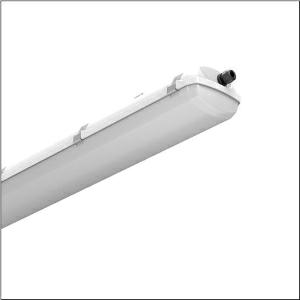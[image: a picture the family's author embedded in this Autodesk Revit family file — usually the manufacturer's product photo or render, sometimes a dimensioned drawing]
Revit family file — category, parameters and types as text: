
# Revit family: monsun_r__ex_51fxb17p670a3g_589b
name_source: partatom
category: Lighting Fixtures
units: mm (PartAtom-declared; Revit-internal decimal feet)

## family parameters
Cut with Voids When Loaded = No
Host = Face
Light Source = No
Part Type = Normal
Room Calculation Point = No
Round Connector Dimension = Use Diameter
Shared = No

## types (1)
- --- (1 x LED, 7310 lm, 44 W, 6500K)
    Apparent Load = 44 VA
    CIE Flux Codes = 61 86 97 100 100
    Color Rendering = 80
    Color Temperature = 6500K
    Default Elevation = 1800 mm
    Description = Monsun® Ex, damp-proof luminaire, primary optical cover: cover, of PC, UV-stabilised, opal, light emission: direct distribution, primary light characteristic: symmetric, installation type: surface-mounted, LED, rated luminous flux: 7.310lm, luminous efficacy: 167lm/W, light colour: 865, colour temperature: 6500K, control gear: ECG, with terminal, 3+1-pole, max. 2.5mm², through-wiring: 6x 2.5mm², mains connection: 220..240V, AC, 50/60Hz, rated input power: 44W, control gear: single battery element, housing, of PC, light grey (RAL 7035), incl. blind plug, incl. 1x Ex cable gland M20 for cable diameter 7..12mm with sealing, length: 1.580mm, width: 155mm, height: 105mm, clip for enclosure, of stainless steel, protection rating (complete): IP66, insulation class (complete): insulation class I (protective earthing), certification: CE, explosion class: zone2,22 II 3G Ex nR IIC T6 GC, II 3D Ex tc IIIC T80°C Dc, impact resistance: IK10, permissible operating ambient temperature: 0..+40°C, LABS conformity tested according to VDMA 24364:2018-05, contact your sales advisor before using the luminaires in applications with unclear chemical exposure, large temperature fluctuations or condensation-forming humidity, packaging unit: 1 piece
    Height = 105 mm
    Lamp = 1 x LED
    Lamp Light Flux = 7310 lm
    Lamp Power = 44 W
    Lamp count = 1
    Length = 1580 mm
    Luminous efficacy = 166 lm/W
    Manufacturer = Siteco
    ModVariant = No
    Model = 51FXB17P670A3G
    Mounting Place = Ceiling
    Mounting Type = Surface mounted
    Number of Poles = 1
    OnlyDefault = Yes
    Power Factor = 1
    Product Name = Monsun® Ex
    Product group = damp-proof luminaire
    ProductGroupID = 301
    Protection Class = Protection class I
    Protection Degree = IP 66
    RLX_Detail_Level = 1
    RLX_Emergency_Light_Flux = 0 lm
    RLX_Emergency_Type = 0
    RLX_Emergency_Type_DB = No
    RlxData = <blob elided: 41685 chars, md5=f67fe839>
    Socket = socket
    Standby Power = 0 W
    System Light Flux = 7310 lm
    System Power = 44 W
    Type Comments = -
    Type Image = l_1258882.jpg
    URL = http://relux.com
    VarID = @adj_031685
    Voltage = 0 V
    Weight = 0.00 kg
    Width = 155 mm

## geometry (parser evidence)
native form markers: Blend x4, Sweep x10
no freeform markers — native parametric forms only
